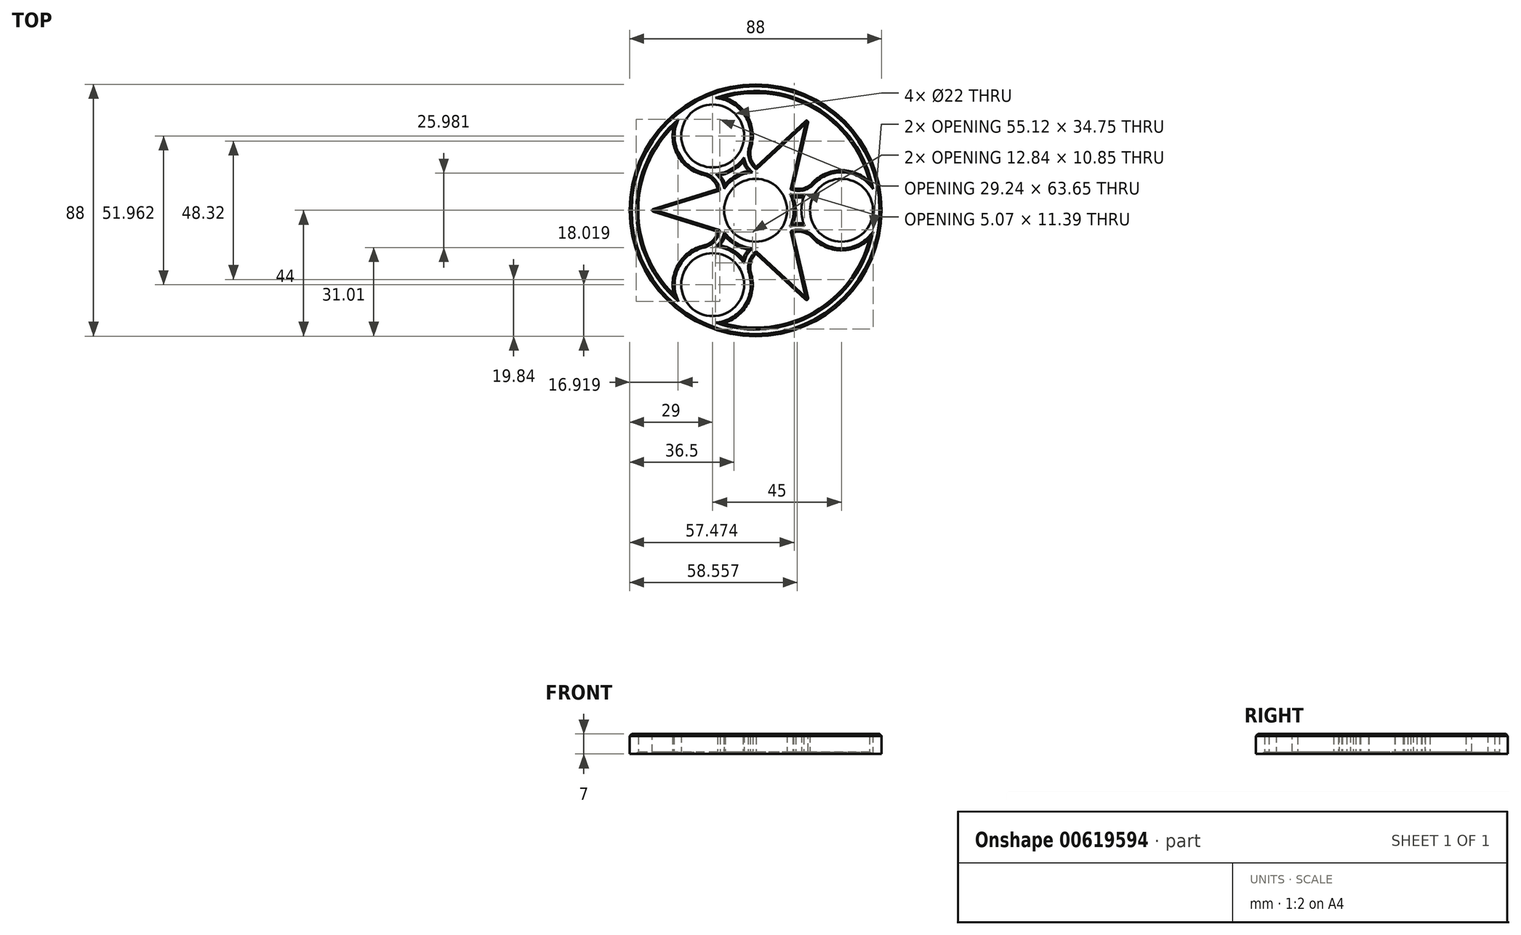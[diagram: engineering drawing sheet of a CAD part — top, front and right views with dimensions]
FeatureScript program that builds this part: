
annotation { "Feature Type Name" : "Feature", "Feature Type Description" : "" }
export const myFeature = defineFeature(function(context is Context, id is Id, definition is map)
    precondition{}
    {
        {
            var Q0;
            Q0=qCreatedBy(makeId("Top.planeOp"),FACE);
            var sketch = newSketch(context, id + "F0", { "sketchPlane" : qUnion([Q0])});
            skCircle(sketch, "E0", {"center": v(0, 0) * mm, "radius": 11 * mm});
            skCircle(sketch, "E1", {"center": v(0, 0) * mm, "radius": 30 * mm, "construction": true});
            skCircle(sketch, "E2", {"center": v(30, 0) * mm, "radius": 11 * mm});
            skCircle(sketch, "E3", {"center": v(0, 0) * mm, "radius": 32 * mm, "construction": true});
            skLineSegment(sketch, "E4", {"start": v(30, 0) * mm, "end": v(19.92, 25.05) * mm, "construction": true});
            skArc(sketch, "E5.0", {"start": v(13.2, -4.64) * mm, "mid": v(14, 0) * mm, "end": v(13.2, 4.64) * mm});
            skArc(sketch, "E6", {"start": v(13.06, 7.77) * mm, "mid": v(16.66, 7.69) * mm, "end": v(19.76, 9.54) * mm});
            skArc(sketch, "E7.0", {"start": v(13.2, 4.64) * mm, "mid": v(15, 4.47) * mm, "end": v(16.8, 4.64) * mm});
            skArc(sketch, "E8.MirrorCS", {"start": v(13.2, -4.64) * mm, "mid": v(15, -4.47) * mm, "end": v(16.8, -4.64) * mm});
            skArc(sketch, "E9.MirrorCS", {"start": v(13.06, -7.77) * mm, "mid": v(16.66, -7.69) * mm, "end": v(19.76, -9.54) * mm});
            skArc(sketch, "E10.trimOffspring", {"start": v(16.8, 4.64) * mm, "mid": v(16, 0) * mm, "end": v(16.8, -4.64) * mm});
            skLineSegment(sketch, "E11", {"start": v(19.76, 9.54) * mm, "end": v(19.76, 9.54) * mm});
            skLineSegment(sketch, "E12", {"start": v(-1.61, -21.88) * mm, "end": v(-1.61, -21.88) * mm});
            skCircle(sketch, "E13", {"center": v(0, 0) * mm, "radius": 44 * mm});
            skArc(sketch, "E14", {"start": v(39.75, 10.05) * mm, "mid": v(20.5, 35.5) * mm, "end": v(-11.17, 39.45) * mm});
            skLineSegment(sketch, "E15", {"start": v(0, 0) * mm, "end": v(30.87, 53.47) * mm, "construction": true});
            skLineSegment(sketch, "E16", {"start": v(0, 0) * mm, "end": v(64.32, 0) * mm, "construction": true});
            skCircle(sketch, "E17", {"center": v(0, 0) * mm, "radius": 37.32 * mm, "construction": true});
            skLineSegment(sketch, "E18", {"start": v(18.66, 32.32) * mm, "end": v(13.06, 7.77) * mm});
            skLineSegment(sketch, "E19.MirrorCS", {"start": v(18.66, 32.32) * mm, "end": v(0.2, 15.2) * mm});
            skArc(sketch, "E20.1.0", {"start": v(-1.61, 21.88) * mm, "mid": v(-2.7, 32.67) * mm, "end": v(-11.17, 39.45) * mm});
            skCircle(sketch, "E20.1.1", {"center": v(-15, 25.98) * mm, "radius": 11 * mm});
            skArc(sketch, "E20.1.2", {"start": v(0.2, 15.2) * mm, "mid": v(-1.67, 18.27) * mm, "end": v(-1.61, 21.88) * mm});
            skArc(sketch, "E20.1.3", {"start": v(-2.58, 13.76) * mm, "mid": v(-3.63, 15.23) * mm, "end": v(-4.37, 16.86) * mm});
            skArc(sketch, "E20.1.4", {"start": v(-2.58, 13.76) * mm, "mid": v(-7, 12.12) * mm, "end": v(-10.63, 9.12) * mm});
            skArc(sketch, "E20.1.5", {"start": v(-13.26, 7.42) * mm, "mid": v(-15, 10.59) * mm, "end": v(-18.14, 12.34) * mm});
            skArc(sketch, "E20.1.6", {"start": v(-10.63, 9.12) * mm, "mid": v(-11.37, 10.75) * mm, "end": v(-12.42, 12.22) * mm});
            skLineSegment(sketch, "E20.1.8", {"start": v(-37.32, 0) * mm, "end": v(-13.26, 7.42) * mm});
            skLineSegment(sketch, "E20.1.9", {"start": v(-37.32, 0) * mm, "end": v(-13.26, -7.42) * mm});
            skArc(sketch, "E20.2.0", {"start": v(-11.17, -39.45) * mm, "mid": v(-2.7, -32.67) * mm, "end": v(-1.61, -21.88) * mm});
            skCircle(sketch, "E20.2.1", {"center": v(-15, -25.98) * mm, "radius": 11 * mm});
            skArc(sketch, "E20.2.2", {"start": v(-13.26, -7.42) * mm, "mid": v(-15, -10.59) * mm, "end": v(-18.14, -12.34) * mm});
            skArc(sketch, "E20.2.3", {"start": v(-10.63, -9.12) * mm, "mid": v(-11.37, -10.75) * mm, "end": v(-12.42, -12.22) * mm});
            skArc(sketch, "E20.2.4", {"start": v(-10.63, -9.12) * mm, "mid": v(-7, -12.12) * mm, "end": v(-2.58, -13.76) * mm});
            skArc(sketch, "E20.2.5", {"start": v(0.2, -15.2) * mm, "mid": v(-1.67, -18.27) * mm, "end": v(-1.61, -21.88) * mm});
            skArc(sketch, "E20.2.6", {"start": v(-2.58, -13.76) * mm, "mid": v(-3.63, -15.23) * mm, "end": v(-4.37, -16.86) * mm});
            skLineSegment(sketch, "E20.2.8", {"start": v(18.66, -32.32) * mm, "end": v(0.2, -15.2) * mm});
            skLineSegment(sketch, "E20.2.9", {"start": v(18.66, -32.32) * mm, "end": v(13.06, -7.77) * mm});
            skPoint(sketch, "E21.orphan", {"position": v(10.24, 9.54) * mm});
            skPoint(sketch, "E22.orphan", {"position": v(3.14, 13.64) * mm});
            skArc(sketch, "E23.trimOffspring", {"start": v(19.76, -9.54) * mm, "mid": v(29.65, -14) * mm, "end": v(39.75, -10.05) * mm});
            skArc(sketch, "E24.trimOffspring", {"start": v(39.75, 10.05) * mm, "mid": v(29.65, 14) * mm, "end": v(19.76, 9.54) * mm});
            skArc(sketch, "E25.trimOffspring", {"start": v(-12.42, 12.22) * mm, "mid": v(-8, 13.86) * mm, "end": v(-4.37, 16.86) * mm});
            skArc(sketch, "E26.trimOffspring", {"start": v(-28.58, 29.4) * mm, "mid": v(-41, 0) * mm, "end": v(-28.58, -29.4) * mm});
            skArc(sketch, "E27.trimOffspring", {"start": v(-28.58, 29.4) * mm, "mid": v(-26.94, 18.68) * mm, "end": v(-18.14, 12.34) * mm});
            skPoint(sketch, "E28.orphan", {"position": v(-13.39, -4.1) * mm});
            skArc(sketch, "E29.trimOffspring", {"start": v(-11.17, -39.45) * mm, "mid": v(20.5, -35.5) * mm, "end": v(39.75, -10.05) * mm});
            skArc(sketch, "E30.trimOffspring", {"start": v(-4.37, -16.86) * mm, "mid": v(-8, -13.86) * mm, "end": v(-12.42, -12.22) * mm});
            skArc(sketch, "E31.trimOffspring", {"start": v(-18.14, -12.34) * mm, "mid": v(-26.94, -18.68) * mm, "end": v(-28.58, -29.4) * mm});
            skPoint(sketch, "E32.orphan", {"position": v(10.24, -9.54) * mm});
            skSolve(sketch);
        }
        {
            var Q0;
            Q0=makeQuery(id+"F0.imprint","IMPRINT",FACE,{"disambiguationData":[TD([[makeQuery(id+"F0.imprint","IMPRINT",EDGE,{"derivedFrom":sQuery(id+"F0.wireOp",EDGE,"E0")}),-1.0]])]});
            extrude(context, id + "F1", {"entities" : qUnion([Q0]), "endBound" : BoundingType.SYMMETRIC, "depth" : 7 * mm, "offsetDistance" : 25 * mm});
        }
        {
            var Q0;
            Q0=makeQuery(id+"F1.opExtrude","CAP_EDGE",EDGE,{"disambiguationData":[OSD([sQuery(id+"F0.wireOp",EDGE,"E26.trimOffspring")])],"isStart":false});
            var Q1;
            Q1=makeQuery(id+"F1.opExtrude","CAP_EDGE",EDGE,{"disambiguationData":[OSD([sQuery(id+"F0.wireOp",EDGE,"E20.1.9")])],"isStart":false});
            var Q2;
            Q2=makeQuery(id+"F1.opExtrude","CAP_EDGE",EDGE,{"disambiguationData":[OSD([sQuery(id+"F0.wireOp",EDGE,"E20.1.8")])],"isStart":false});
            var Q3;
            Q3=makeQuery(id+"F1.opExtrude","CAP_EDGE",EDGE,{"disambiguationData":[OSD([sQuery(id+"F0.wireOp",EDGE,"E20.1.5")])],"isStart":false});
            var Q4;
            Q4=makeQuery(id+"F1.opExtrude","CAP_EDGE",EDGE,{"disambiguationData":[OSD([sQuery(id+"F0.wireOp",EDGE,"E27.trimOffspring")])],"isStart":false});
            var Q5;
            Q5=makeQuery(id+"F1.opExtrude","CAP_EDGE",EDGE,{"disambiguationData":[OSD([sQuery(id+"F0.wireOp",EDGE,"E31.trimOffspring")])],"isStart":false});
            var Q6;
            Q6=makeQuery(id+"F1.opExtrude","CAP_EDGE",EDGE,{"disambiguationData":[OSD([sQuery(id+"F0.wireOp",EDGE,"E20.2.2")])],"isStart":false});
            var Q7;
            Q7=makeQuery(id+"F1.opExtrude","CAP_EDGE",EDGE,{"disambiguationData":[OSD([sQuery(id+"F0.wireOp",EDGE,"E30.trimOffspring")])],"isStart":false});
            var Q8;
            Q8=makeQuery(id+"F1.opExtrude","CAP_EDGE",EDGE,{"disambiguationData":[OSD([sQuery(id+"F0.wireOp",EDGE,"E20.2.3")])],"isStart":false});
            var Q9;
            Q9=makeQuery(id+"F1.opExtrude","CAP_EDGE",EDGE,{"disambiguationData":[OSD([sQuery(id+"F0.wireOp",EDGE,"E20.2.4")])],"isStart":false});
            var Q10;
            Q10=makeQuery(id+"F1.opExtrude","CAP_EDGE",EDGE,{"disambiguationData":[OSD([sQuery(id+"F0.wireOp",EDGE,"E20.2.6")])],"isStart":false});
            var Q11;
            Q11=makeQuery(id+"F1.opExtrude","CAP_EDGE",EDGE,{"disambiguationData":[OSD([sQuery(id+"F0.wireOp",EDGE,"E20.2.5")])],"isStart":false});
            var Q12;
            Q12=makeQuery(id+"F1.opExtrude","CAP_EDGE",EDGE,{"disambiguationData":[OSD([sQuery(id+"F0.wireOp",EDGE,"E20.2.8")])],"isStart":false});
            var Q13;
            Q13=makeQuery(id+"F1.opExtrude","CAP_EDGE",EDGE,{"disambiguationData":[OSD([sQuery(id+"F0.wireOp",EDGE,"E29.trimOffspring")])],"isStart":false});
            var Q14;
            Q14=makeQuery(id+"F1.opExtrude","CAP_EDGE",EDGE,{"disambiguationData":[OSD([sQuery(id+"F0.wireOp",EDGE,"E23.trimOffspring")])],"isStart":false});
            var Q15;
            Q15=makeQuery(id+"F1.opExtrude","CAP_EDGE",EDGE,{"disambiguationData":[OSD([sQuery(id+"F0.wireOp",EDGE,"E20.2.9")])],"isStart":false});
            var Q16;
            Q16=makeQuery(id+"F1.opExtrude","CAP_EDGE",EDGE,{"disambiguationData":[OSD([sQuery(id+"F0.wireOp",EDGE,"E9.MirrorCS")])],"isStart":false});
            var Q17;
            Q17=makeQuery(id+"F1.opExtrude","CAP_EDGE",EDGE,{"disambiguationData":[OSD([sQuery(id+"F0.wireOp",EDGE,"E20.2.0")])],"isStart":false});
            var Q18;
            Q18=makeQuery(id+"F1.opExtrude","CAP_EDGE",EDGE,{"disambiguationData":[OSD([sQuery(id+"F0.wireOp",EDGE,"E10.trimOffspring")])],"isStart":false});
            var Q19;
            Q19=makeQuery(id+"F1.opExtrude","CAP_EDGE",EDGE,{"disambiguationData":[OSD([sQuery(id+"F0.wireOp",EDGE,"E5.0")])],"isStart":false});
            var Q20;
            Q20=makeQuery(id+"F1.opExtrude","CAP_EDGE",EDGE,{"disambiguationData":[OSD([sQuery(id+"F0.wireOp",EDGE,"E7.0")])],"isStart":false});
            var Q21;
            Q21=makeQuery(id+"F1.opExtrude","CAP_EDGE",EDGE,{"disambiguationData":[OSD([sQuery(id+"F0.wireOp",EDGE,"E8.MirrorCS")])],"isStart":false});
            var Q22;
            Q22=makeQuery(id+"F1.opExtrude","CAP_EDGE",EDGE,{"disambiguationData":[OSD([sQuery(id+"F0.wireOp",EDGE,"E18")])],"isStart":false});
            var Q23;
            Q23=makeQuery(id+"F1.opExtrude","CAP_EDGE",EDGE,{"disambiguationData":[OSD([sQuery(id+"F0.wireOp",EDGE,"E24.trimOffspring")])],"isStart":false});
            var Q24;
            Q24=makeQuery(id+"F1.opExtrude","CAP_EDGE",EDGE,{"disambiguationData":[OSD([sQuery(id+"F0.wireOp",EDGE,"E6")])],"isStart":false});
            var Q25;
            Q25=makeQuery(id+"F1.opExtrude","CAP_EDGE",EDGE,{"disambiguationData":[OSD([sQuery(id+"F0.wireOp",EDGE,"E14")])],"isStart":false});
            var Q26;
            Q26=makeQuery(id+"F1.opExtrude","CAP_EDGE",EDGE,{"disambiguationData":[OSD([sQuery(id+"F0.wireOp",EDGE,"E20.1.0")])],"isStart":false});
            var Q27;
            Q27=makeQuery(id+"F1.opExtrude","CAP_EDGE",EDGE,{"disambiguationData":[OSD([sQuery(id+"F0.wireOp",EDGE,"E20.1.2")])],"isStart":false});
            var Q28;
            Q28=makeQuery(id+"F1.opExtrude","CAP_EDGE",EDGE,{"disambiguationData":[OSD([sQuery(id+"F0.wireOp",EDGE,"E19.MirrorCS")])],"isStart":false});
            var Q29;
            Q29=makeQuery(id+"F1.opExtrude","CAP_EDGE",EDGE,{"disambiguationData":[OSD([sQuery(id+"F0.wireOp",EDGE,"E25.trimOffspring")])],"isStart":false});
            var Q30;
            Q30=makeQuery(id+"F1.opExtrude","CAP_EDGE",EDGE,{"disambiguationData":[OSD([sQuery(id+"F0.wireOp",EDGE,"E20.1.4")])],"isStart":false});
            var Q31;
            Q31=makeQuery(id+"F1.opExtrude","CAP_EDGE",EDGE,{"disambiguationData":[OSD([sQuery(id+"F0.wireOp",EDGE,"E20.1.3")])],"isStart":false});
            var Q32;
            Q32=makeQuery(id+"F1.opExtrude","CAP_EDGE",EDGE,{"disambiguationData":[OSD([sQuery(id+"F0.wireOp",EDGE,"E20.1.6")])],"isStart":false});
            var Q33;
            Q33=makeQuery(id+"F1.opExtrude","CAP_EDGE",EDGE,{"disambiguationData":[OSD([sQuery(id+"F0.wireOp",EDGE,"E13")])],"isStart":false});
            var Q34;
            Q34=makeQuery(id+"F1.opExtrude","CAP_EDGE",EDGE,{"disambiguationData":[OSD([sQuery(id+"F0.wireOp",EDGE,"E20.1.0")])],"isStart":true});
            var Q35;
            Q35=makeQuery(id+"F1.opExtrude","CAP_EDGE",EDGE,{"disambiguationData":[OSD([sQuery(id+"F0.wireOp",EDGE,"E20.1.2")])],"isStart":true});
            var Q36;
            Q36=makeQuery(id+"F1.opExtrude","CAP_EDGE",EDGE,{"disambiguationData":[OSD([sQuery(id+"F0.wireOp",EDGE,"E19.MirrorCS")])],"isStart":true});
            var Q37;
            Q37=makeQuery(id+"F1.opExtrude","CAP_EDGE",EDGE,{"disambiguationData":[OSD([sQuery(id+"F0.wireOp",EDGE,"E18")])],"isStart":true});
            var Q38;
            Q38=makeQuery(id+"F1.opExtrude","CAP_EDGE",EDGE,{"disambiguationData":[OSD([sQuery(id+"F0.wireOp",EDGE,"E6")])],"isStart":true});
            var Q39;
            Q39=makeQuery(id+"F1.opExtrude","CAP_EDGE",EDGE,{"disambiguationData":[OSD([sQuery(id+"F0.wireOp",EDGE,"E24.trimOffspring")])],"isStart":true});
            var Q40;
            Q40=makeQuery(id+"F1.opExtrude","CAP_EDGE",EDGE,{"disambiguationData":[OSD([sQuery(id+"F0.wireOp",EDGE,"E14")])],"isStart":true});
            var Q41;
            Q41=makeQuery(id+"F1.opExtrude","CAP_EDGE",EDGE,{"disambiguationData":[OSD([sQuery(id+"F0.wireOp",EDGE,"E10.trimOffspring")])],"isStart":true});
            var Q42;
            Q42=makeQuery(id+"F1.opExtrude","CAP_EDGE",EDGE,{"disambiguationData":[OSD([sQuery(id+"F0.wireOp",EDGE,"E7.0")])],"isStart":true});
            var Q43;
            Q43=makeQuery(id+"F1.opExtrude","CAP_EDGE",EDGE,{"disambiguationData":[OSD([sQuery(id+"F0.wireOp",EDGE,"E5.0")])],"isStart":true});
            var Q44;
            Q44=makeQuery(id+"F1.opExtrude","CAP_EDGE",EDGE,{"disambiguationData":[OSD([sQuery(id+"F0.wireOp",EDGE,"E8.MirrorCS")])],"isStart":true});
            var Q45;
            Q45=makeQuery(id+"F1.opExtrude","CAP_EDGE",EDGE,{"disambiguationData":[OSD([sQuery(id+"F0.wireOp",EDGE,"E9.MirrorCS")])],"isStart":true});
            var Q46;
            Q46=makeQuery(id+"F1.opExtrude","CAP_EDGE",EDGE,{"disambiguationData":[OSD([sQuery(id+"F0.wireOp",EDGE,"E23.trimOffspring")])],"isStart":true});
            var Q47;
            Q47=makeQuery(id+"F1.opExtrude","CAP_EDGE",EDGE,{"disambiguationData":[OSD([sQuery(id+"F0.wireOp",EDGE,"E20.2.9")])],"isStart":true});
            var Q48;
            Q48=makeQuery(id+"F1.opExtrude","CAP_EDGE",EDGE,{"disambiguationData":[OSD([sQuery(id+"F0.wireOp",EDGE,"E29.trimOffspring")])],"isStart":true});
            var Q49;
            Q49=makeQuery(id+"F1.opExtrude","CAP_EDGE",EDGE,{"disambiguationData":[OSD([sQuery(id+"F0.wireOp",EDGE,"E20.2.8")])],"isStart":true});
            var Q50;
            Q50=makeQuery(id+"F1.opExtrude","CAP_EDGE",EDGE,{"disambiguationData":[OSD([sQuery(id+"F0.wireOp",EDGE,"E20.2.5")])],"isStart":true});
            var Q51;
            Q51=makeQuery(id+"F1.opExtrude","CAP_EDGE",EDGE,{"disambiguationData":[OSD([sQuery(id+"F0.wireOp",EDGE,"E20.2.0")])],"isStart":true});
            var Q52;
            Q52=makeQuery(id+"F1.opExtrude","CAP_EDGE",EDGE,{"disambiguationData":[OSD([sQuery(id+"F0.wireOp",EDGE,"E26.trimOffspring")])],"isStart":true});
            var Q53;
            Q53=makeQuery(id+"F1.opExtrude","CAP_EDGE",EDGE,{"disambiguationData":[OSD([sQuery(id+"F0.wireOp",EDGE,"E31.trimOffspring")])],"isStart":true});
            var Q54;
            Q54=makeQuery(id+"F1.opExtrude","CAP_EDGE",EDGE,{"disambiguationData":[OSD([sQuery(id+"F0.wireOp",EDGE,"E30.trimOffspring")])],"isStart":true});
            var Q55;
            Q55=makeQuery(id+"F1.opExtrude","CAP_EDGE",EDGE,{"disambiguationData":[OSD([sQuery(id+"F0.wireOp",EDGE,"E20.2.4")])],"isStart":true});
            var Q56;
            Q56=makeQuery(id+"F1.opExtrude","CAP_EDGE",EDGE,{"disambiguationData":[OSD([sQuery(id+"F0.wireOp",EDGE,"E20.2.3")])],"isStart":true});
            var Q57;
            Q57=makeQuery(id+"F1.opExtrude","CAP_EDGE",EDGE,{"disambiguationData":[OSD([sQuery(id+"F0.wireOp",EDGE,"E20.2.6")])],"isStart":true});
            var Q58;
            Q58=makeQuery(id+"F1.opExtrude","CAP_EDGE",EDGE,{"disambiguationData":[OSD([sQuery(id+"F0.wireOp",EDGE,"E20.1.9")])],"isStart":true});
            var Q59;
            Q59=makeQuery(id+"F1.opExtrude","CAP_EDGE",EDGE,{"disambiguationData":[OSD([sQuery(id+"F0.wireOp",EDGE,"E20.2.2")])],"isStart":true});
            var Q60;
            Q60=makeQuery(id+"F1.opExtrude","CAP_EDGE",EDGE,{"disambiguationData":[OSD([sQuery(id+"F0.wireOp",EDGE,"E20.1.8")])],"isStart":true});
            var Q61;
            Q61=makeQuery(id+"F1.opExtrude","CAP_EDGE",EDGE,{"disambiguationData":[OSD([sQuery(id+"F0.wireOp",EDGE,"E20.1.5")])],"isStart":true});
            var Q62;
            Q62=makeQuery(id+"F1.opExtrude","CAP_EDGE",EDGE,{"disambiguationData":[OSD([sQuery(id+"F0.wireOp",EDGE,"E27.trimOffspring")])],"isStart":true});
            var Q63;
            Q63=makeQuery(id+"F1.opExtrude","CAP_EDGE",EDGE,{"disambiguationData":[OSD([sQuery(id+"F0.wireOp",EDGE,"E25.trimOffspring")])],"isStart":true});
            var Q64;
            Q64=makeQuery(id+"F1.opExtrude","CAP_EDGE",EDGE,{"disambiguationData":[OSD([sQuery(id+"F0.wireOp",EDGE,"E20.1.4")])],"isStart":true});
            var Q65;
            Q65=makeQuery(id+"F1.opExtrude","CAP_EDGE",EDGE,{"disambiguationData":[OSD([sQuery(id+"F0.wireOp",EDGE,"E20.1.6")])],"isStart":true});
            var Q66;
            Q66=makeQuery(id+"F1.opExtrude","CAP_EDGE",EDGE,{"disambiguationData":[OSD([sQuery(id+"F0.wireOp",EDGE,"E20.1.3")])],"isStart":true});
            chamfer(context, id + "F2", {"entities" : qUnion([Q0, Q1, Q2, Q3, Q4, Q5, Q6, Q7, Q8, Q9, Q10, Q11, Q12, Q13, Q14, Q15, Q16, Q17, Q18, Q19, Q20, Q21, Q22, Q23, Q24, Q25, Q26, Q27, Q28, Q29, Q30, Q31, Q32, Q33, Q34, Q35, Q36, Q37, Q38, Q39, Q40, Q41, Q42, Q43, Q44, Q45, Q46, Q47, Q48, Q49, Q50, Q51, Q52, Q53, Q54, Q55, Q56, Q57, Q58, Q59, Q60, Q61, Q62, Q63, Q64, Q65, Q66]), "width" : .7 * mm, "tangentPropagation" : true});
        }
        {
            var Q0;
            Q0=makeQuery(id+"F1.opExtrude","SWEPT_EDGE",EDGE,{"disambiguationData":[OSD([sQuery(id+"F0.wireOp",EDGE,"E20.2.8"),sQuery(id+"F0.wireOp",EDGE,"E20.2.9")])]});
            var Q1;
            Q1=makeQuery(id+"F1.opExtrude","SWEPT_EDGE",EDGE,{"disambiguationData":[OSD([sQuery(id+"F0.wireOp",EDGE,"E20.1.8"),sQuery(id+"F0.wireOp",EDGE,"E20.1.9")])]});
            var Q2;
            Q2=makeQuery(id+"F1.opExtrude","SWEPT_EDGE",EDGE,{"disambiguationData":[OSD([sQuery(id+"F0.wireOp",EDGE,"E18"),sQuery(id+"F0.wireOp",EDGE,"E19.MirrorCS")])]});
            fillet(context, id + "F3", {"entities" : qUnion([Q0, Q1, Q2]), "radius" : .5 * mm, "tangentPropagation" : true, "allowEdgeOverflow" : false});
        }
    });
